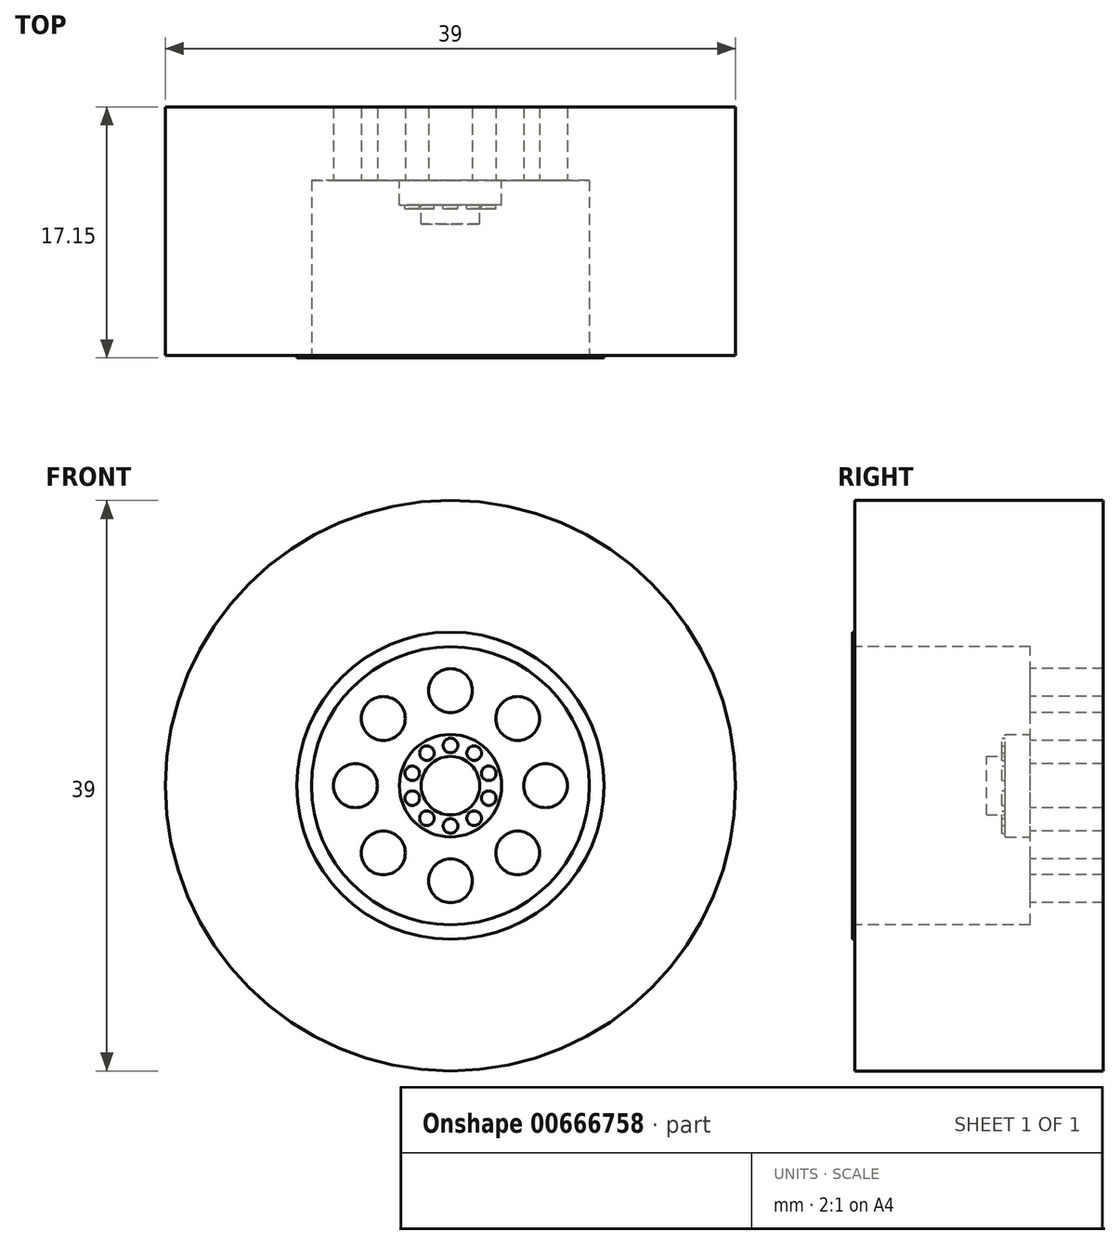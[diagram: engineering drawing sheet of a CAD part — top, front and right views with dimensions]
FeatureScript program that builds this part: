
annotation { "Feature Type Name" : "Feature", "Feature Type Description" : "" }
export const myFeature = defineFeature(function(context is Context, id is Id, definition is map)
    precondition{}
    {
        {
            var Q0;
            Q0=qCreatedBy(makeId("Front.planeOp"),FACE);
            var sketch = newSketch(context, id + "F0", { "sketchPlane" : qUnion([Q0])});
            skCircle(sketch, "E0", {"center": v(0, 0) * mm, "radius": 19.5 * mm});
            skSolve(sketch);
        }
        {
            var Q0;
            Q0=makeQuery(id+"F0.imprint","IMPRINT",FACE,{"disambiguationData":[TD([[makeQuery(id+"F0.imprint","IMPRINT",EDGE,{"derivedFrom":sQuery(id+"F0.wireOp",EDGE,"E0")}),1.0]])]});
            extrude(context, id + "F1", {"entities" : qUnion([Q0]), "depth" : 17 * mm, "offsetDistance" : 25 * mm});
        }
        {
            var Q0;
            Q0=makeQuery(id+"F1.opExtrude","CAP_FACE",FACE,{"disambiguationData":[OSD([sQuery(id+"F0.wireOp",EDGE,"E0")])],"isStart":false});
            var sketch = newSketch(context, id + "F2", { "sketchPlane" : qUnion([Q0])});
            skCircle(sketch, "E1", {"center": v(0, 0) * mm, "radius": 10.5 * mm});
            skCircle(sketch, "E2", {"center": v(0, 0) * mm, "radius": 9.5 * mm});
            skSolve(sketch);
        }
        {
            var Q0;
            Q0=makeQuery(id+"F2.imprint","IMPRINT",FACE,{"disambiguationData":[TD([[makeQuery(id+"F2.imprint","IMPRINT",EDGE,{"derivedFrom":sQuery(id+"F2.wireOp",EDGE,"E2")}),1.0]])]});
            extrude(context, id + "F3", {"entities" : qUnion([Q0]), "operationType" : NewBodyOperationType.REMOVE, "oppositeDirection" : true, "depth" : 12 * mm, "offsetDistance" : 25 * mm});
        }
        {
            var Q0;
            Q0=makeQuery(id+"F1.opExtrude","CAP_FACE",FACE,{"disambiguationData":[OSD([sQuery(id+"F0.wireOp",EDGE,"E0")])],"isStart":false});
            var sketch = newSketch(context, id + "F4", { "sketchPlane" : qUnion([Q0])});
            skCircle(sketch, "E3", {"center": v(0, 0) * mm, "radius": 10.5 * mm});
            skSolve(sketch);
        }
        {
            var Q0;
            Q0=makeQuery(id+"F4.imprint","IMPRINT",FACE,{"disambiguationData":[TD([[makeQuery(id+"F4.imprint","IMPRINT",EDGE,{"derivedFrom":sQuery(id+"F4.wireOp",EDGE,"E3")}),1.0]])]});
            extrude(context, id + "F5", {"entities" : qUnion([Q0]), "operationType" : NewBodyOperationType.ADD, "depth" : .15 * mm, "offsetDistance" : 25 * mm});
        }
        {
            var Q0;
            Q0=makeQuery(id+"F3.boolean.opBoolean","COPY",FACE,{"derivedFrom":makeQuery(id+"F3.opExtrude","CAP_FACE",FACE,{"disambiguationData":[OSD([sQuery(id+"F2.wireOp",EDGE,"E2")])],"isStart":false})});
            var sketch = newSketch(context, id + "F6", { "sketchPlane" : qUnion([Q0])});
            skCircle(sketch, "E4", {"center": v(0, 0) * mm, "radius": 2 * mm});
            skCircle(sketch, "E5", {"center": v(0, 0) * mm, "radius": 3.5 * mm});
            skSolve(sketch);
        }
        {
            var Q0;
            Q0=makeQuery(id+"F6.imprint","IMPRINT",FACE,{"disambiguationData":[TD([[makeQuery(id+"F6.imprint","IMPRINT",EDGE,{"derivedFrom":sQuery(id+"F6.wireOp",EDGE,"E4")}),1.0]])]});
            extrude(context, id + "F7", {"entities" : qUnion([Q0]), "operationType" : NewBodyOperationType.ADD, "depth" : 3 * mm, "offsetDistance" : 25 * mm});
        }
        {
            var Q0;
            Q0=makeQuery(id+"F3.boolean.opBoolean","COPY",FACE,{"derivedFrom":makeQuery(id+"F3.opExtrude","CAP_FACE",FACE,{"disambiguationData":[OSD([sQuery(id+"F2.wireOp",EDGE,"E2")])],"isStart":false})});
            var sketch = newSketch(context, id + "F8", { "sketchPlane" : qUnion([Q0])});
            skCircle(sketch, "E6", {"center": v(0, 0) * mm, "radius": 3.5 * mm});
            skSolve(sketch);
        }
        {
            var Q0;
            Q0=makeQuery(id+"F8.imprint","IMPRINT",FACE,{"disambiguationData":[TD([[makeQuery(id+"F8.imprint","IMPRINT",EDGE,{"derivedFrom":sQuery(id+"F8.wireOp",EDGE,"E6")}),1.0]])]});
            extrude(context, id + "F9", {"entities" : qUnion([Q0]), "operationType" : NewBodyOperationType.ADD, "depth" : 1.7 * mm, "offsetDistance" : 25 * mm});
        }
        {
            var Q0;
            Q0=makeQuery(id+"F9.opExtrude","CAP_FACE",FACE,{"disambiguationData":[OSD([sQuery(id+"F6.wireOp",EDGE,"E4"),sQuery(id+"F8.wireOp",EDGE,"E6")])],"isStart":false});
            var sketch = newSketch(context, id + "F10", { "sketchPlane" : qUnion([Q0])});
            skCircle(sketch, "E7", {"center": v(0, 2.75) * mm, "radius": 0.5 * mm});
            skCircle(sketch, "E8.1.0", {"center": v(-1.62, 2.22) * mm, "radius": 0.5 * mm});
            skCircle(sketch, "E8.2.0", {"center": v(-2.62, 0.85) * mm, "radius": 0.5 * mm});
            skCircle(sketch, "E8.3.0", {"center": v(-2.62, -0.85) * mm, "radius": 0.5 * mm});
            skCircle(sketch, "E8.4.0", {"center": v(-1.62, -2.22) * mm, "radius": 0.5 * mm});
            skCircle(sketch, "E8.5.0", {"center": v(0, -2.75) * mm, "radius": 0.5 * mm});
            skCircle(sketch, "E8.6.0", {"center": v(1.62, -2.22) * mm, "radius": 0.5 * mm});
            skCircle(sketch, "E8.7.0", {"center": v(2.62, -0.85) * mm, "radius": 0.5 * mm});
            skCircle(sketch, "E8.8.0", {"center": v(2.62, 0.85) * mm, "radius": 0.5 * mm});
            skCircle(sketch, "E8.9.0", {"center": v(1.62, 2.22) * mm, "radius": 0.5 * mm});
            skPoint(sketch, "E8.center", {"position": v(0, 0) * mm});
            skSolve(sketch);
        }
        {
            var Q0;
            Q0=makeQuery(id+"F10.imprint","IMPRINT",FACE,{"disambiguationData":[TD([[makeQuery(id+"F10.imprint","IMPRINT",EDGE,{"derivedFrom":sQuery(id+"F10.wireOp",EDGE,"E7")}),1.0]])]});
            var Q1;
            Q1=makeQuery(id+"F10.imprint","IMPRINT",FACE,{"disambiguationData":[TD([[makeQuery(id+"F10.imprint","IMPRINT",EDGE,{"derivedFrom":sQuery(id+"F10.wireOp",EDGE,"E8.9.0")}),1.0]])]});
            var Q2;
            Q2=makeQuery(id+"F10.imprint","IMPRINT",FACE,{"disambiguationData":[TD([[makeQuery(id+"F10.imprint","IMPRINT",EDGE,{"derivedFrom":sQuery(id+"F10.wireOp",EDGE,"E8.7.0")}),1.0]])]});
            var Q3;
            Q3=makeQuery(id+"F10.imprint","IMPRINT",FACE,{"disambiguationData":[TD([[makeQuery(id+"F10.imprint","IMPRINT",EDGE,{"derivedFrom":sQuery(id+"F10.wireOp",EDGE,"E8.6.0")}),1.0]])]});
            var Q4;
            Q4=makeQuery(id+"F10.imprint","IMPRINT",FACE,{"disambiguationData":[TD([[makeQuery(id+"F10.imprint","IMPRINT",EDGE,{"derivedFrom":sQuery(id+"F10.wireOp",EDGE,"E8.5.0")}),1.0]])]});
            var Q5;
            Q5=makeQuery(id+"F10.imprint","IMPRINT",FACE,{"disambiguationData":[TD([[makeQuery(id+"F10.imprint","IMPRINT",EDGE,{"derivedFrom":sQuery(id+"F10.wireOp",EDGE,"E8.8.0")}),1.0]])]});
            var Q6;
            Q6=makeQuery(id+"F10.imprint","IMPRINT",FACE,{"disambiguationData":[TD([[makeQuery(id+"F10.imprint","IMPRINT",EDGE,{"derivedFrom":sQuery(id+"F10.wireOp",EDGE,"E8.4.0")}),1.0]])]});
            var Q7;
            Q7=makeQuery(id+"F10.imprint","IMPRINT",FACE,{"disambiguationData":[TD([[makeQuery(id+"F10.imprint","IMPRINT",EDGE,{"derivedFrom":sQuery(id+"F10.wireOp",EDGE,"E8.3.0")}),1.0]])]});
            var Q8;
            Q8=makeQuery(id+"F10.imprint","IMPRINT",FACE,{"disambiguationData":[TD([[makeQuery(id+"F10.imprint","IMPRINT",EDGE,{"derivedFrom":sQuery(id+"F10.wireOp",EDGE,"E8.2.0")}),1.0]])]});
            var Q9;
            Q9=makeQuery(id+"F10.imprint","IMPRINT",FACE,{"disambiguationData":[TD([[makeQuery(id+"F10.imprint","IMPRINT",EDGE,{"derivedFrom":sQuery(id+"F10.wireOp",EDGE,"E8.1.0")}),1.0]])]});
            extrude(context, id + "F11", {"entities" : qUnion([Q0, Q1, Q2, Q3, Q4, Q5, Q6, Q7, Q8, Q9]), "operationType" : NewBodyOperationType.ADD, "depth" : .25 * mm, "offsetDistance" : 25 * mm});
        }
        {
            var Q0;
            Q0=makeQuery(id+"F3.boolean.opBoolean","COPY",FACE,{"derivedFrom":makeQuery(id+"F3.opExtrude","CAP_FACE",FACE,{"disambiguationData":[OSD([sQuery(id+"F2.wireOp",EDGE,"E2")])],"isStart":false})});
            var sketch = newSketch(context, id + "F12", { "sketchPlane" : qUnion([Q0])});
            skCircle(sketch, "E9", {"center": v(0, 6.5) * mm, "radius": 1.5 * mm});
            skCircle(sketch, "E10.1.0", {"center": v(-4.6, 4.6) * mm, "radius": 1.5 * mm});
            skCircle(sketch, "E10.2.0", {"center": v(-6.5, 0) * mm, "radius": 1.5 * mm});
            skCircle(sketch, "E10.3.0", {"center": v(-4.6, -4.6) * mm, "radius": 1.5 * mm});
            skCircle(sketch, "E10.4.0", {"center": v(0, -6.5) * mm, "radius": 1.5 * mm});
            skCircle(sketch, "E10.5.0", {"center": v(4.6, -4.6) * mm, "radius": 1.5 * mm});
            skCircle(sketch, "E10.6.0", {"center": v(6.5, 0) * mm, "radius": 1.5 * mm});
            skCircle(sketch, "E10.7.0", {"center": v(4.6, 4.6) * mm, "radius": 1.5 * mm});
            skPoint(sketch, "E10.center", {"position": v(0, 0) * mm});
            skSolve(sketch);
        }
        {
            var Q0;
            Q0=makeQuery(id+"F12.imprint","IMPRINT",FACE,{"disambiguationData":[TD([[makeQuery(id+"F12.imprint","IMPRINT",EDGE,{"derivedFrom":sQuery(id+"F12.wireOp",EDGE,"E9")}),1.0]])]});
            var Q1;
            Q1=makeQuery(id+"F12.imprint","IMPRINT",FACE,{"disambiguationData":[TD([[makeQuery(id+"F12.imprint","IMPRINT",EDGE,{"derivedFrom":sQuery(id+"F12.wireOp",EDGE,"E10.7.0")}),1.0]])]});
            var Q2;
            Q2=makeQuery(id+"F12.imprint","IMPRINT",FACE,{"disambiguationData":[TD([[makeQuery(id+"F12.imprint","IMPRINT",EDGE,{"derivedFrom":sQuery(id+"F12.wireOp",EDGE,"E10.6.0")}),1.0]])]});
            var Q3;
            Q3=makeQuery(id+"F12.imprint","IMPRINT",FACE,{"disambiguationData":[TD([[makeQuery(id+"F12.imprint","IMPRINT",EDGE,{"derivedFrom":sQuery(id+"F12.wireOp",EDGE,"E10.1.0")}),1.0]])]});
            var Q4;
            Q4=makeQuery(id+"F12.imprint","IMPRINT",FACE,{"disambiguationData":[TD([[makeQuery(id+"F12.imprint","IMPRINT",EDGE,{"derivedFrom":sQuery(id+"F12.wireOp",EDGE,"E10.2.0")}),1.0]])]});
            var Q5;
            Q5=makeQuery(id+"F12.imprint","IMPRINT",FACE,{"disambiguationData":[TD([[makeQuery(id+"F12.imprint","IMPRINT",EDGE,{"derivedFrom":sQuery(id+"F12.wireOp",EDGE,"E10.3.0")}),1.0]])]});
            var Q6;
            Q6=makeQuery(id+"F12.imprint","IMPRINT",FACE,{"disambiguationData":[TD([[makeQuery(id+"F12.imprint","IMPRINT",EDGE,{"derivedFrom":sQuery(id+"F12.wireOp",EDGE,"E10.5.0")}),1.0]])]});
            var Q7;
            Q7=makeQuery(id+"F12.imprint","IMPRINT",FACE,{"disambiguationData":[TD([[makeQuery(id+"F12.imprint","IMPRINT",EDGE,{"derivedFrom":sQuery(id+"F12.wireOp",EDGE,"E10.4.0")}),1.0]])]});
            extrude(context, id + "F13", {"entities" : qUnion([Q0, Q1, Q2, Q3, Q4, Q5, Q6, Q7]), "operationType" : NewBodyOperationType.REMOVE, "oppositeDirection" : true, "depth" : 25 * mm, "offsetDistance" : 25 * mm});
        }
    });
